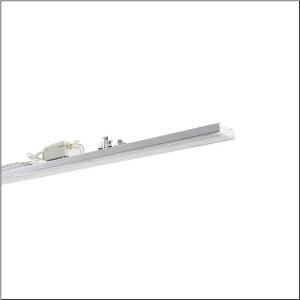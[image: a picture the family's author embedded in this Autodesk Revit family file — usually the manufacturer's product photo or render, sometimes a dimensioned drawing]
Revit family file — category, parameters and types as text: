
# Revit family: licross_r__21_recessed_mo_52te19dv4e5g_2993
name_source: partatom
category: Lighting Fixtures
units: mm (PartAtom-declared; Revit-internal decimal feet)

## family parameters
Cut with Voids When Loaded = No
Host = Face
Light Source = No
Part Type = Normal
Room Calculation Point = No
Round Connector Dimension = Use Diameter
Shared = No

## types (1)
- --- (1 x LED, 14780 lm, 85.3 W, 4000K)
    Apparent Load = 85 VA
    CIE Flux Codes = 55 90 98 100 100
    Color Rendering = 80
    Color Temperature = 4000K
    Default Elevation = 1800 mm
    Description = Licross® 21 Recessed MO, luminaire insert, of sheet steel, galvanised, coil coated, white, length: 2.250mm, width: 66mm, height: 67mm, LED rated luminous flux: 14.780lm, light colour: 840, control gear: DALI 2, with plug, 5-pole, with phase selection, mains connection: 220..240V, AC, 50/60Hz, rated input power: 85W, halogen-free wiring, primary light control with lens, of plastic, primary optical cover: cover, of PMMA, light emission: direct distribution, primary light characteristic: double asymmetric, protection rating (complete): IP54, insulation class (complete): insulation class I (protective earthing), certification: CE, ENEC, VDE, UKCA, protection symbol: D if used in an environment with non-conductive dust loads with corresponding accessories, impact resistance: IK06, permissible ambient temperature for indoor applications: -25..+35°C, corresponds to IFS (International Featured Standards) requirements for safety and quality in the food industry, reducing of maximum allowable ambient temperature of 5°C with ceiling mounting, LABS conformity tested according to VDMA 24364:2018-05, packaging unit: 1 piece
    Height = 58 mm
    Lamp = 1 x LED
    Lamp Light Flux = 14780 lm
    Lamp Power = 85.3 W
    Lamp count = 1
    Length = 2250 mm
    Luminous efficacy = 173 lm/W
    Manufacturer = Siteco
    ModVariant = No
    Model = 52TE19DV4E5G
    Mounting Place = Ceiling
    Mounting Type = Pendant
    Number of Poles = 1
    OnlyDefault = Yes
    Power Factor = 1
    Product Name = Licross® 21 Recessed MO
    Product group = luminaire insert
    ProductGroupID = 901
    Protection Class = Protection class I
    Protection Degree = IP 54
    RLX_Detail_Level = 1
    RLX_Emergency_Light_Flux = 0 lm
    RLX_Emergency_Type = 0
    RLX_Emergency_Type_DB = No
    RlxData = <blob elided: 29485 chars, md5=f7605e25>
    Socket = socket
    Standby Power = 0 W
    System Light Flux = 14780 lm
    System Power = 85 W
    Type Comments = factory setting: luminous flux: 100 % | dim-lin: 254 | 390 mA
    Type Image = l_1296930.jpg
    URL = http://relux.com
    VarID = @adj_059619
    Voltage = 0 V
    Weight = 0.00 kg
    Width = 66 mm

## geometry (parser evidence)
native form markers: Blend x4, Sweep x9
no freeform markers — native parametric forms only
